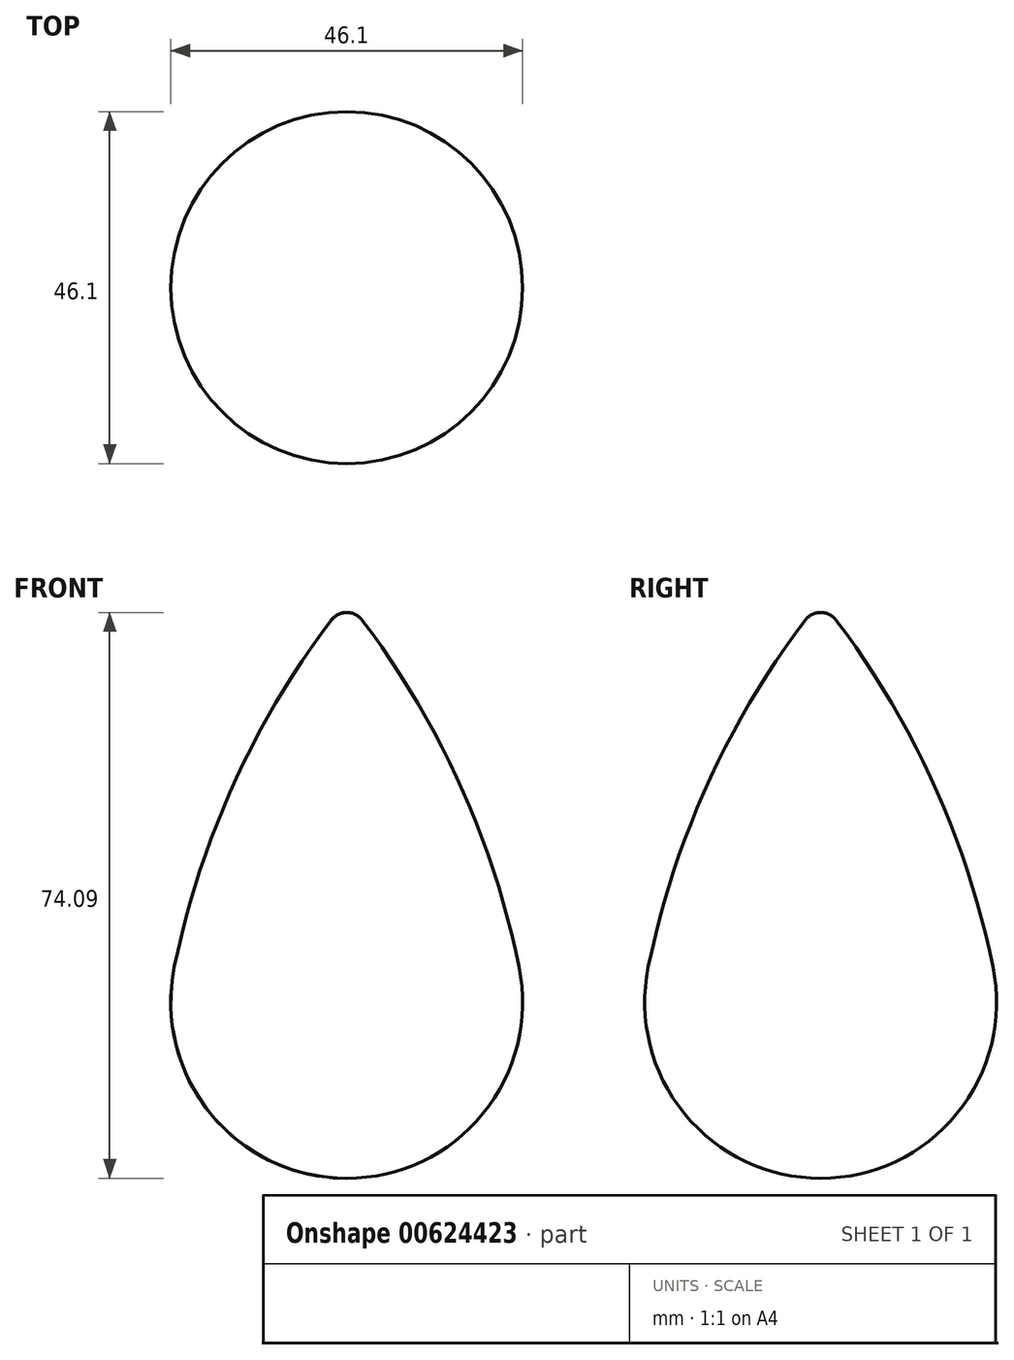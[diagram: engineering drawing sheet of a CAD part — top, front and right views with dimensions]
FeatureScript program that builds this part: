
annotation { "Feature Type Name" : "Feature", "Feature Type Description" : "" }
export const myFeature = defineFeature(function(context is Context, id is Id, definition is map)
    precondition{}
    {
        {
            var Q0;
            Q0=qCreatedBy(makeId("Front.planeOp"),FACE);
            var sketch = newSketch(context, id + "F0", { "sketchPlane" : qUnion([Q0])});
            skArc(sketch, "E0", {"start": v(-22.59, 4.6) * mm, "mid": v(-17.85, -14.59) * mm, "end": v(0, -23.05) * mm});
            skLineSegment(sketch, "E1", {"start": v(0, 52.62) * mm, "end": v(0, 51.04) * mm});
            skArc(sketch, "E2", {"start": v(-2.02, 50.04) * mm, "mid": v(-14.87, 28.47) * mm, "end": v(-22.59, 4.6) * mm});
            skPoint(sketch, "E3.visualSharp", {"position": v(0, 52.62) * mm});
            skLineSegment(sketch, "E4", {"start": v(0, 51.04) * mm, "end": v(0, -23.05) * mm});
            skArc(sketch, "E5", {"start": v(0, 51.04) * mm, "mid": v(-1.13, 50.78) * mm, "end": v(-2.02, 50.04) * mm});
            skSolve(sketch);
        }
        {
            var Q0;
            Q0=makeQuery(id+"F0.imprint","IMPRINT",FACE,{"disambiguationData":[TD([[makeQuery(id+"F0.imprint","IMPRINT",EDGE,{"derivedFrom":sQuery(id+"F0.wireOp",EDGE,"E0")}),1.0]])]});
            var Q1;
            Q1=sQuery(id+"F0.wireOp",EDGE,"E4");
            revolve(context, id + "F1", {"entities" : qUnion([Q0]), "axis" : qUnion([Q1]), "revolveType" : RevolveType.FULL});
        }
    });
